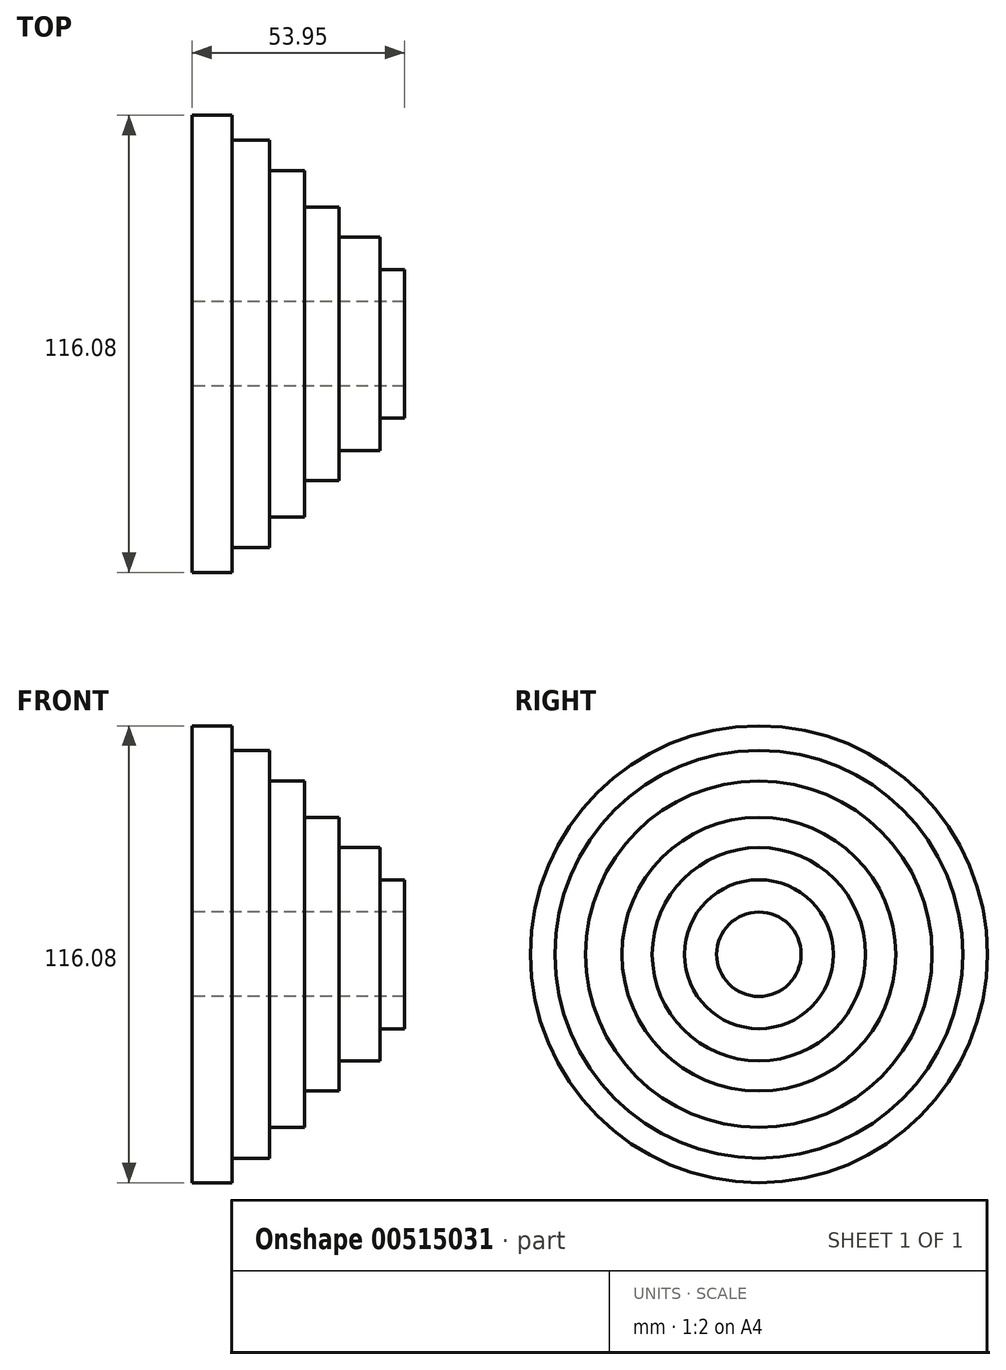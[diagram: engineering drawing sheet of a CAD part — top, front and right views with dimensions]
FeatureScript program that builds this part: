
annotation { "Feature Type Name" : "Feature", "Feature Type Description" : "" }
export const myFeature = defineFeature(function(context is Context, id is Id, definition is map)
    precondition{}
    {
        {
            var Q0;
            Q0=qCreatedBy(makeId("Front.planeOp"),FACE);
            var sketch = newSketch(context, id + "F0", { "sketchPlane" : qUnion([Q0])});
            skLineSegment(sketch, "E0.bottom", {"start": v(-28.61, 10.72) * mm, "end": v(-18.47, 10.72) * mm});
            skLineSegment(sketch, "E0.top", {"start": v(-28.61, 58.04) * mm, "end": v(-18.47, 58.04) * mm});
            skLineSegment(sketch, "E0.left", {"start": v(-28.61, 10.72) * mm, "end": v(-28.61, 58.04) * mm});
            skLineSegment(sketch, "E0.right", {"start": v(-18.47, 10.72) * mm, "end": v(-18.47, 58.04) * mm});
            skLineSegment(sketch, "E1.bottom", {"start": v(-18.47, 10.72) * mm, "end": v(-8.98, 10.72) * mm});
            skLineSegment(sketch, "E1.top", {"start": v(-18.47, 51.8) * mm, "end": v(-8.98, 51.8) * mm});
            skLineSegment(sketch, "E1.left", {"start": v(-18.47, 10.72) * mm, "end": v(-18.47, 51.8) * mm});
            skLineSegment(sketch, "E1.right", {"start": v(-8.98, 10.72) * mm, "end": v(-8.98, 51.8) * mm});
            skLineSegment(sketch, "E2.bottom", {"start": v(-8.98, 10.72) * mm, "end": v(0, 10.72) * mm});
            skLineSegment(sketch, "E2.top", {"start": v(-8.98, 44) * mm, "end": v(0, 44) * mm});
            skLineSegment(sketch, "E2.left", {"start": v(-8.98, 10.72) * mm, "end": v(-8.98, 44) * mm});
            skLineSegment(sketch, "E2.right", {"start": v(0, 10.72) * mm, "end": v(0, 44) * mm});
            skLineSegment(sketch, "E3.bottom", {"start": v(0, 10.72) * mm, "end": v(8.7, 10.72) * mm});
            skLineSegment(sketch, "E3.top", {"start": v(0, 34.77) * mm, "end": v(8.7, 34.77) * mm});
            skLineSegment(sketch, "E3.left", {"start": v(0, 10.72) * mm, "end": v(0, 34.77) * mm});
            skLineSegment(sketch, "E3.right", {"start": v(8.7, 10.72) * mm, "end": v(8.7, 34.77) * mm});
            skLineSegment(sketch, "E4.bottom", {"start": v(8.7, 10.72) * mm, "end": v(19.1, 10.72) * mm});
            skLineSegment(sketch, "E4.top", {"start": v(8.7, 27.1) * mm, "end": v(19.1, 27.1) * mm});
            skLineSegment(sketch, "E4.left", {"start": v(8.7, 10.72) * mm, "end": v(8.7, 27.1) * mm});
            skLineSegment(sketch, "E4.right", {"start": v(19.1, 10.72) * mm, "end": v(19.1, 27.1) * mm});
            skPoint(sketch, "E5.oppositeSnap0", {"position": v(19.1, 18.91) * mm});
            skLineSegment(sketch, "E5.bottom", {"start": v(19.1, 10.72) * mm, "end": v(25.34, 10.72) * mm});
            skLineSegment(sketch, "E5.top", {"start": v(19.1, 18.91) * mm, "end": v(25.34, 18.91) * mm});
            skLineSegment(sketch, "E5.left", {"start": v(19.1, 10.72) * mm, "end": v(19.1, 18.91) * mm});
            skLineSegment(sketch, "E5.right", {"start": v(25.34, 10.72) * mm, "end": v(25.34, 18.91) * mm});
            skLineSegment(sketch, "E6.bottom", {"start": v(-51.23, 0) * mm, "end": v(55.11, 0) * mm});
            skLineSegment(sketch, "E6.top", {"start": v(-51.23, 0) * mm, "end": v(55.11, 0) * mm});
            skLineSegment(sketch, "E6.left", {"start": v(-51.23, 0) * mm, "end": v(-51.23, 0) * mm});
            skLineSegment(sketch, "E6.right", {"start": v(55.11, 0) * mm, "end": v(55.11, 0) * mm});
            skSolve(sketch);
        }
        {
            var Q0;
            Q0 = qSketchRegion(id + "F0", true);
            var Q1;
            Q1=sQuery(id+"F0.wireOp",EDGE,"E6.top");
            revolve(context, id + "F1", {"entities" : qUnion([Q0]), "axis" : qUnion([Q1]), "revolveType" : RevolveType.FULL});
        }
    });
